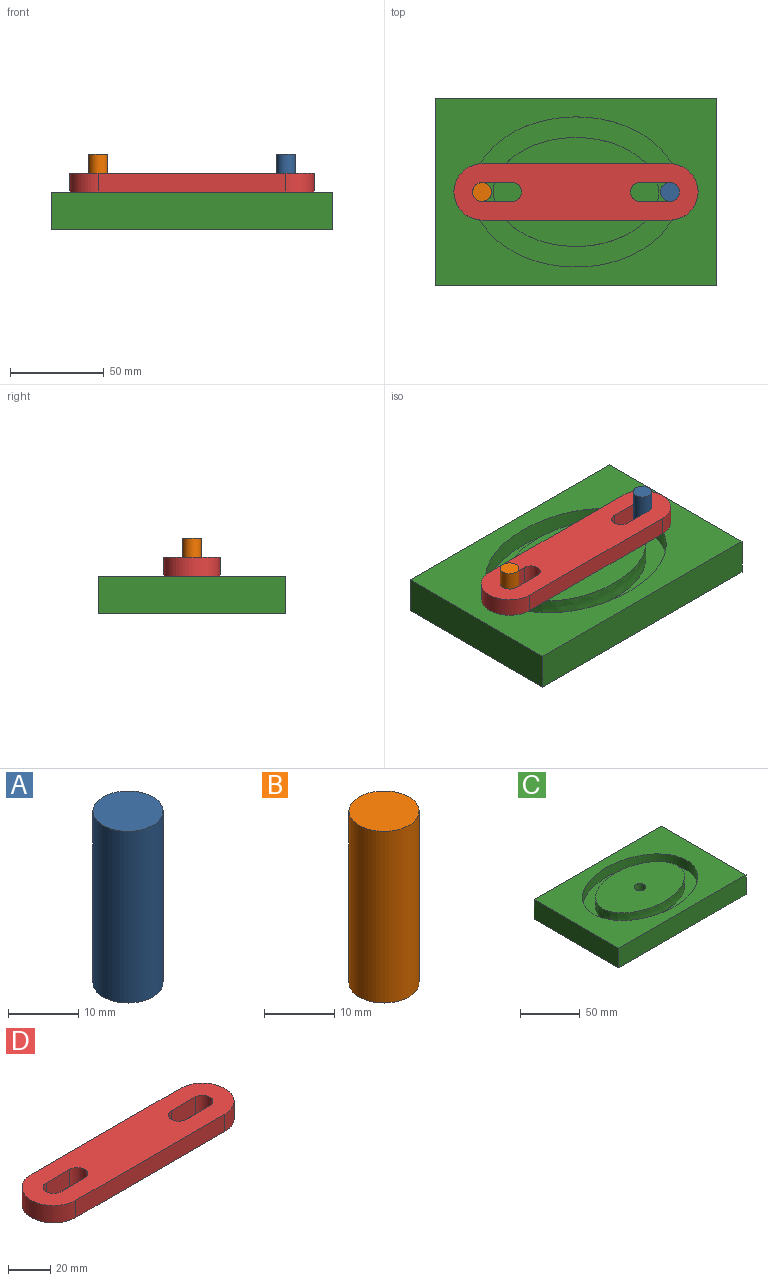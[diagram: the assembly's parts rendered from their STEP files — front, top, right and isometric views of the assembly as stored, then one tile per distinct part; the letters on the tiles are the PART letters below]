
ASSEMBLY  parts=4 mates=3
PART A: 3 faces, bbox 10x10x30 mm
  f0: cylinder r=5mm len=30mm, axis (0,0,-1), area 942.5mm2, adj f1,f2
  f1: plane 10x10mm, normal (0,0,1), area 78.5mm2, adj f0
  f2: plane 10x10mm, normal (0,0,-1), area 78.5mm2, adj f0
PART B: 3 faces, bbox 10x10x30 mm
  f0: cylinder r=5mm len=30mm, axis (0,0,-1), area 942.5mm2, adj f1,f2
  f1: plane 10x10mm, normal (0,0,1), area 78.5mm2, adj f0
  f2: plane 10x10mm, normal (0,0,-1), area 78.5mm2, adj f0
PART C: 12 faces, bbox 150x100x20 mm
  f0: plane 100x20mm, normal (1,0,0), area 2000mm2, adj f1,f3,f4,f5
  f1: plane 150x20mm, normal (0,1,0), area 3000mm2, adj f0,f2,f4,f5
  f2: plane 100x20mm, normal (-1,0,0), area 2000mm2, adj f1,f3,f4,f5
  f3: plane 150x20mm, normal (0,-1,0), area 3000mm2, adj f0,f2,f4,f5
  f4: plane 150x100mm, normal (0,0,1), area 8088.5mm2, adj f0,f1,f2,f3,f7
  f5: plane 150x100mm, normal (0,0,-1), area 15000mm2, adj f0,f1,f2,f3
  f6: extruded ~88x58mm, area 2312.4mm2, adj f8,f9
  f7: extruded ~110x80mm, area 3003.1mm2, adj f4,f8
  f8: plane 110x80mm, normal (0,0,1), area 2924.2mm2, adj f6,f7
  f9: plane 88x58mm, normal (0,0,1), area 3909.1mm2, adj f6,f10
  f10: cylinder r=5mm len=10mm, axis (0,0,1), area 314.2mm2, adj f9,f11
  f11: plane 10x10mm, normal (0,0,1), area 78.5mm2, adj f10
PART D: 16 faces, bbox 130x30x20 mm
  f0: cylinder r=5mm len=10mm, axis (0,0,-1), area 157.1mm2, adj f1,f11,f12,f13
  f1: plane 16x10mm, normal (0,-1,0), area 160mm2, adj f0,f2,f12,f13
  f2: cylinder r=5mm len=10mm, axis (0,0,-1), area 157.1mm2, adj f1,f11,f12,f13
  f3: plane 100x10mm, normal (0,1,0), area 1000mm2, adj f4,f9,f12,f13
  f4: cylinder r=15mm len=30mm, axis (0,0,-1), area 471.2mm2, adj f3,f5,f12,f13
  f5: plane 100x10mm, normal (0,-1,0), area 1000mm2, adj f4,f9,f12,f13
  f6: plane 16x10mm, normal (0,-1,0), area 160mm2, adj f7,f10,f12,f13
  f7: cylinder r=5mm len=10mm, axis (0,0,-1), area 157.1mm2, adj f6,f8,f12,f13
  f8: plane 16x10mm, normal (0,1,0), area 160mm2, adj f7,f10,f12,f13
  f9: cylinder r=15mm len=30mm, axis (0,0,-1), area 471.2mm2, adj f3,f5,f12,f13
  f10: cylinder r=5mm len=10mm, axis (0,0,-1), area 157.1mm2, adj f6,f8,f12,f13
  f11: plane 16x10mm, normal (0,1,0), area 160mm2, adj f0,f2,f12,f13
  f12: plane 130x30mm, normal (0,0,1), area 3229.8mm2, adj f0,f1,f2,f3,f4,f5,f6,f7
  f13: plane 130x30mm, normal (0,0,-1), area 3151.2mm2, adj f0,f1,f2,f3,f4,f5,f6,f7
  f14: cylinder r=5mm len=10mm, axis (0,0,1), area 314.2mm2, adj f13,f15
  f15: plane 10x10mm, normal (0,0,-1), area 78.5mm2, adj f14
PLACE A rot(axis=(0,0,1),91.8deg) t=(37.6,-43.71,-22.56)mm
PLACE B rot(axis=(0,0,1),31.3deg) t=(-21.21,32.22,-22.56)mm
PLACE C t=(-13.94,6.26,-22.56)mm fixed
PLACE D rot(axis=(0,0,1),180deg) t=(-13.94,6.26,-22.56)mm
MATE planar A.f0 <-> C.f10  axis (0,0,-1) through (36.06,6.26,-12.56)mm
MATE planar B.f0 <-> C.f8  axis (0,0,-1) through (-63.94,6.26,-12.56)mm
MATE revolute C.f10 <-> D.f14  axis (0,0,1) through (-13.94,6.26,-12.56)mm
